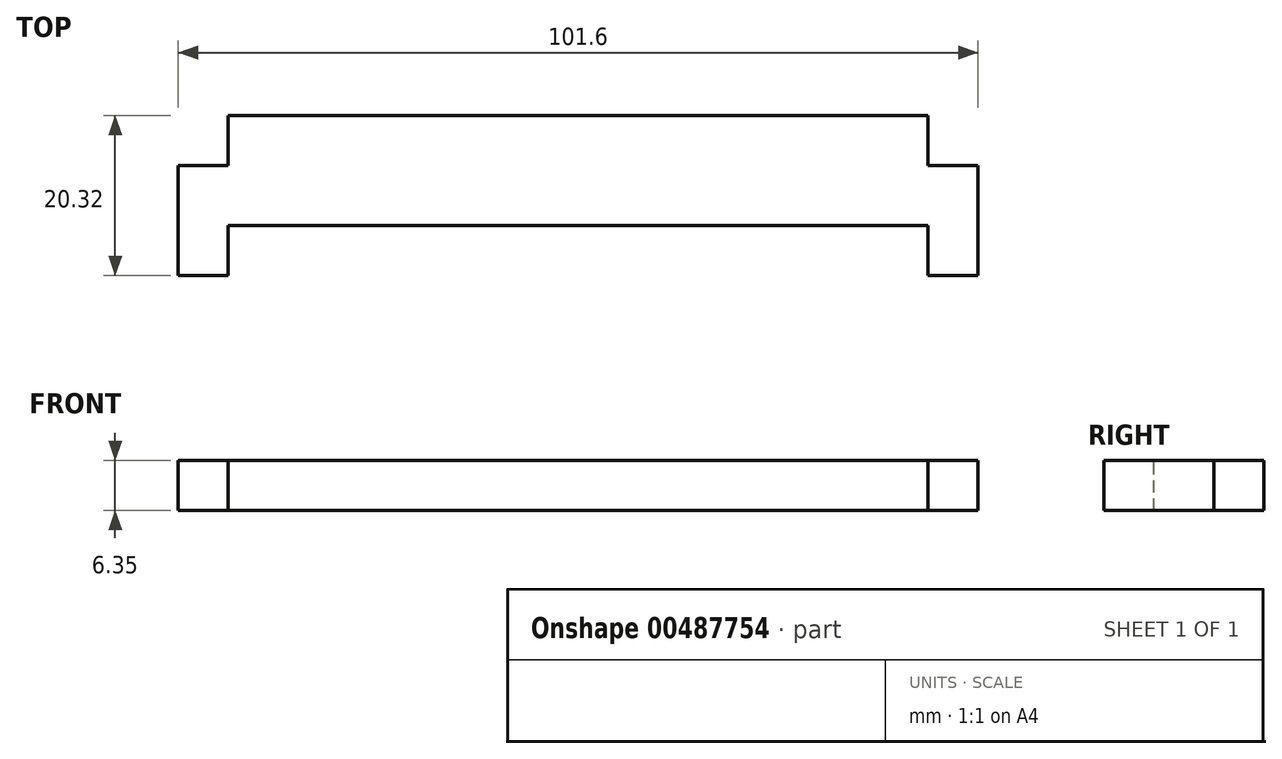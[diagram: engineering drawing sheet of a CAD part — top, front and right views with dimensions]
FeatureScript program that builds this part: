
annotation { "Feature Type Name" : "Feature", "Feature Type Description" : "" }
export const myFeature = defineFeature(function(context is Context, id is Id, definition is map)
    precondition{}
    {
        {
            var Q0;
            Q0=qCreatedBy(makeId("Top.planeOp"),FACE);
            var sketch = newSketch(context, id + "F0", { "sketchPlane" : qUnion([Q0])});
            skLineSegment(sketch, "E0.bottom", {"start": v(-50.8, 10.16) * mm, "end": v(50.8, 10.16) * mm});
            skLineSegment(sketch, "E0.top", {"start": v(-50.8, -10.16) * mm, "end": v(50.8, -10.16) * mm});
            skLineSegment(sketch, "E0.left", {"start": v(-50.8, 10.16) * mm, "end": v(-50.8, -10.16) * mm});
            skLineSegment(sketch, "E0.right", {"start": v(50.8, 10.16) * mm, "end": v(50.8, -10.16) * mm});
            skPoint(sketch, "E0.middle", {"position": v(0, 0) * mm});
            skSolve(sketch);
        }
        {
            var Q0;
            Q0=makeQuery(id+"F0.imprint","IMPRINT",FACE,{"disambiguationData":[TD([[makeQuery(id+"F0.imprint","IMPRINT",EDGE,{"derivedFrom":sQuery(id+"F0.wireOp",EDGE,"E0.bottom")}),-1.0]])]});
            extrude(context, id + "F1", {"entities" : qUnion([Q0]), "depth" : 6.35 * mm});
        }
        {
            var Q0;
            Q0=makeQuery(id+"F1.opExtrude","CAP_FACE",FACE,{"disambiguationData":[OSD([sQuery(id+"F0.wireOp",EDGE,"E0.bottom"),sQuery(id+"F0.wireOp",EDGE,"E0.top"),sQuery(id+"F0.wireOp",EDGE,"E0.left"),sQuery(id+"F0.wireOp",EDGE,"E0.right")])],"isStart":false});
            var sketch = newSketch(context, id + "F2", { "sketchPlane" : qUnion([Q0])});
            skLineSegment(sketch, "E1.bottom", {"start": v(-50.8, 10.16) * mm, "end": v(-44.45, 10.16) * mm});
            skLineSegment(sketch, "E1.top", {"start": v(-50.8, 3.8) * mm, "end": v(-44.45, 3.8) * mm});
            skLineSegment(sketch, "E1.left", {"start": v(-50.8, 10.16) * mm, "end": v(-50.8, 3.8) * mm});
            skLineSegment(sketch, "E1.right", {"start": v(-44.45, 10.16) * mm, "end": v(-44.45, 3.8) * mm});
            skLineSegment(sketch, "E2.bottom", {"start": v(-50.8, -10.16) * mm, "end": v(-44.45, -10.16) * mm});
            skLineSegment(sketch, "E2.top", {"start": v(-50.8, -3.8) * mm, "end": v(-44.45, -3.8) * mm});
            skLineSegment(sketch, "E2.left", {"start": v(-50.8, -10.16) * mm, "end": v(-50.8, -3.8) * mm});
            skLineSegment(sketch, "E2.right", {"start": v(-44.45, -10.16) * mm, "end": v(-44.45, -3.8) * mm});
            skLineSegment(sketch, "E3.bottom", {"start": v(50.8, -10.16) * mm, "end": v(44.45, -10.16) * mm});
            skLineSegment(sketch, "E3.top", {"start": v(50.8, -3.8) * mm, "end": v(44.45, -3.8) * mm});
            skLineSegment(sketch, "E3.left", {"start": v(50.8, -10.16) * mm, "end": v(50.8, -3.8) * mm});
            skLineSegment(sketch, "E3.right", {"start": v(44.45, -10.16) * mm, "end": v(44.45, -3.8) * mm});
            skLineSegment(sketch, "E4.bottom", {"start": v(50.8, 10.16) * mm, "end": v(44.45, 10.16) * mm});
            skLineSegment(sketch, "E4.top", {"start": v(50.8, 3.8) * mm, "end": v(44.45, 3.8) * mm});
            skLineSegment(sketch, "E4.left", {"start": v(50.8, 10.16) * mm, "end": v(50.8, 3.8) * mm});
            skLineSegment(sketch, "E4.right", {"start": v(44.45, 10.16) * mm, "end": v(44.45, 3.8) * mm});
            skLineSegment(sketch, "E5.bottom", {"start": v(-44.45, -3.8) * mm, "end": v(44.45, -3.8) * mm});
            skLineSegment(sketch, "E5.top", {"start": v(-44.45, -10.16) * mm, "end": v(44.45, -10.16) * mm});
            skLineSegment(sketch, "E5.left", {"start": v(-44.45, -3.8) * mm, "end": v(-44.45, -10.16) * mm});
            skLineSegment(sketch, "E5.right", {"start": v(44.45, -3.8) * mm, "end": v(44.45, -10.16) * mm});
            skSolve(sketch);
        }
        {
            var Q0;
            Q0=makeQuery(id+"F2.imprint","IMPRINT",FACE,{"disambiguationData":[TD([[makeQuery(id+"F2.imprint","IMPRINT",EDGE,{"derivedFrom":sQuery(id+"F2.wireOp",EDGE,"E5.bottom")}),-1.0]])]});
            var Q1;
            Q1=makeQuery(id+"F2.imprint","IMPRINT",FACE,{"disambiguationData":[TD([[makeQuery(id+"F2.imprint","IMPRINT",EDGE,{"derivedFrom":sQuery(id+"F2.wireOp",EDGE,"E1.bottom")}),-1.0]])]});
            var Q2;
            Q2=makeQuery(id+"F2.imprint","IMPRINT",FACE,{"disambiguationData":[TD([[makeQuery(id+"F2.imprint","IMPRINT",EDGE,{"derivedFrom":sQuery(id+"F2.wireOp",EDGE,"E4.bottom")}),-1.0]])]});
            extrude(context, id + "F3", {"entities" : qUnion([Q0, Q1, Q2]), "operationType" : NewBodyOperationType.REMOVE, "endBound" : BoundingType.THROUGH_ALL, "oppositeDirection" : true, "depth" : 6.35 * mm});
        }
    });
